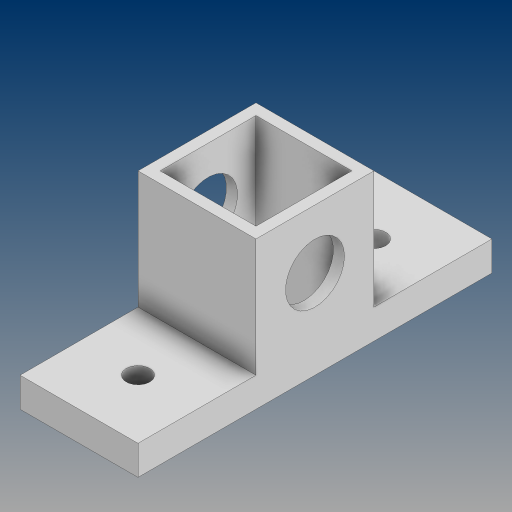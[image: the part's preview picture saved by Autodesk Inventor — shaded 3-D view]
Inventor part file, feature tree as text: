
AUTODESK INVENTOR PART (.ipt)
format: ipt  version: 2024.3 (Build 283343000, 343)  size: 165,376 bytes
history: native  units: in
note: dims shown in document units (in); Inventor stores cm internally (conversion verified against a paired STEP export)
features: sketch x4, extrude x3, projected_geometry x3, hole x1
ambient origin geometry x8: Origin, YZ Plane, XZ Plane, XY Plane, X Axis, Y Axis, Z Axis, Center Point
bodies: Solid1 (feature_tree)
feature tree (11):
  extrude  "Extrusion1"  Depth=3.0in
  extrude  "Extrusion2"  Depth=0.2in
  hole  "Hole1"  [1 undecoded]
  extrude  "Extrusion3"  Depth=1.25in
  sketch  "Sketch1"  dims[d2=1.0in d3=3.0in]
  sketch  "Sketch2"  dims[d4=0.2in d5=0.2in]
  projected_geometry  "Projected Loop1"
  sketch  "Sketch3"  dims[d6=1.0in d7=1.0in]
  projected_geometry  "Projected Loop2"
  sketch  "Sketch4"  dims[d8=0.5in d9=0.5in d10=0.25in d11=0.0in d12=1.0in d13=1.0in d14=1.0in d15=1.0in d16=0.0in d17=0.5in d18=0.5in d19=0.5in d20=1.0in d21=0.375in d22=0.25in d23=0.5635in d24=1.0in d25=0.8108in d26=0.0938in d27=1.25in d28=0.0in d29=0.75in d30=0.375in]
  projected_geometry  "Projected Loop3"
note: 1 required parameter value undecoded (feature->parameter linkage not recoverable at this tier; creation-order binding heuristic only, values carry confidence <= 0.55)
